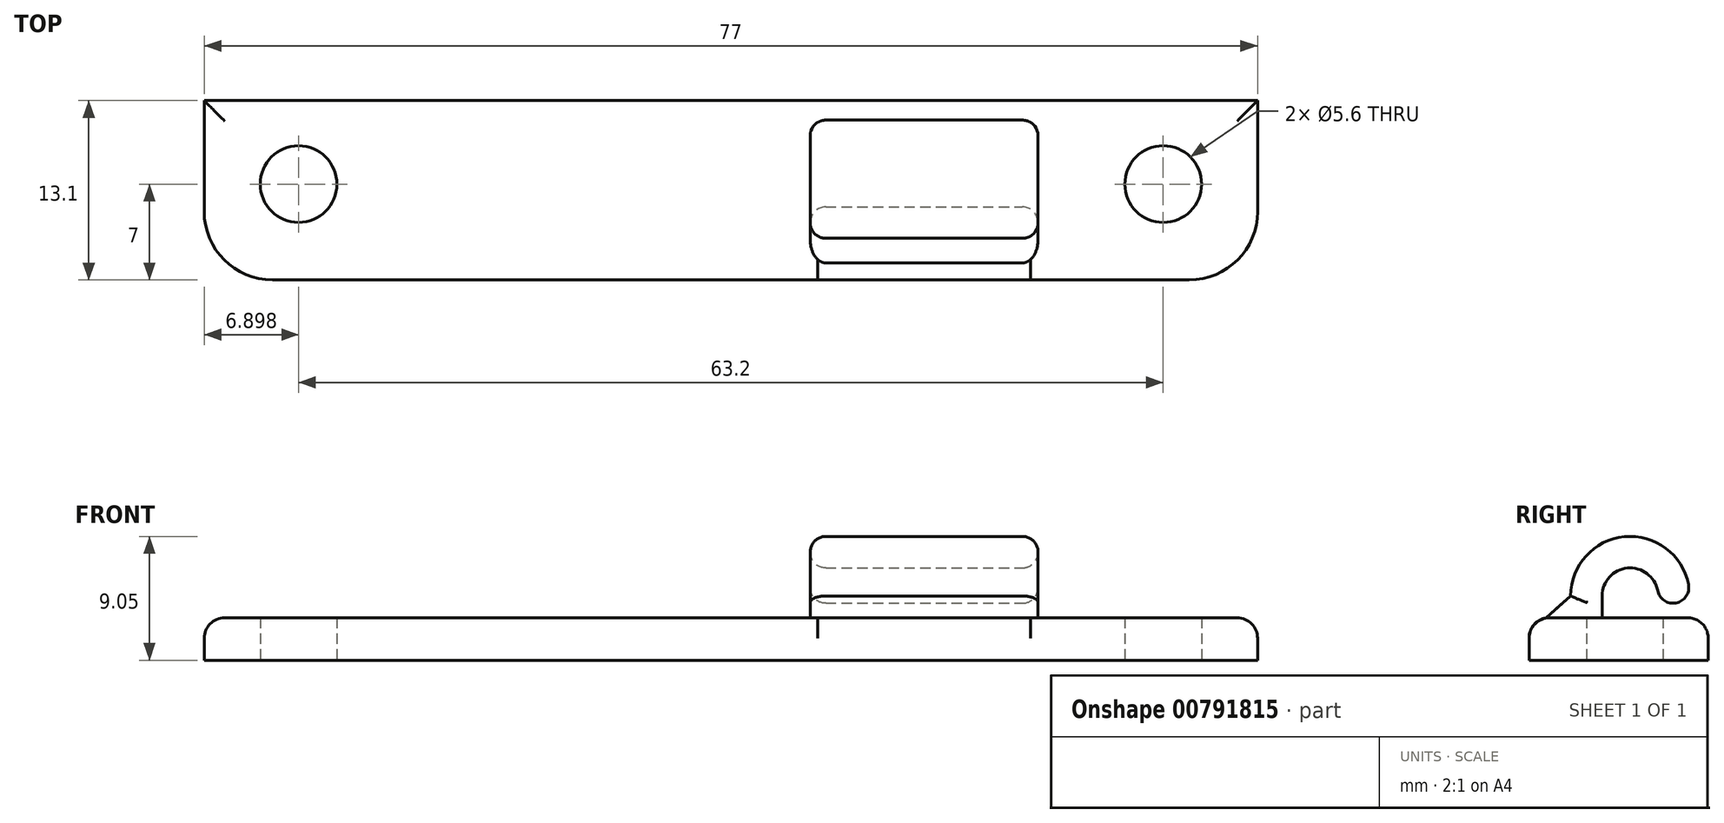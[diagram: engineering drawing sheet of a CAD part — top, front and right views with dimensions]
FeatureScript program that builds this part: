
annotation { "Feature Type Name" : "Feature", "Feature Type Description" : "" }
export const myFeature = defineFeature(function(context is Context, id is Id, definition is map)
    precondition{}
    {
        {
            var Q0;
            Q0=qCreatedBy(makeId("Top.planeOp"),FACE);
            var sketch = newSketch(context, id + "F0", { "sketchPlane" : qUnion([Q0])});
            skLineSegment(sketch, "E0.bottom", {"start": v(-29.06, 27.5) * mm, "end": v(37.94, 27.5) * mm});
            skCircle(sketch, "E1", {"center": v(-27.16, 21.4) * mm, "radius": 2.8 * mm});
            skLineSegment(sketch, "E2", {"start": v(36.74, 27.5) * mm, "end": v(36.74, 21.3) * mm});
            skCircle(sketch, "E3", {"center": v(36.04, 21.4) * mm, "radius": 2.8 * mm});
            skPoint(sketch, "E4.visualSharp", {"position": v(-34.06, 27.5) * mm});
            skPoint(sketch, "E5.visualSharp", {"position": v(42.94, 27.5) * mm});
            skLineSegment(sketch, "E6", {"start": v(-34.06, 27.5) * mm, "end": v(-34.06, 22.5) * mm});
            skLineSegment(sketch, "E7", {"start": v(-29.06, 27.5) * mm, "end": v(-34.06, 27.5) * mm});
            skPoint(sketch, "E8.visualSharp", {"position": v(-34.06, 14.4) * mm});
            skArc(sketch, "E8.filletArc", {"start": v(-34.06, 19.4) * mm, "mid": v(-32.6, 15.86) * mm, "end": v(-29.06, 14.4) * mm});
            skLineSegment(sketch, "E9", {"start": v(37.94, 27.5) * mm, "end": v(42.94, 27.5) * mm});
            skLineSegment(sketch, "E10", {"start": v(42.94, 22.5) * mm, "end": v(42.94, 27.5) * mm});
            skLineSegment(sketch, "E11", {"start": v(-29.06, 14.4) * mm, "end": v(37.94, 14.4) * mm});
            skPoint(sketch, "E12.visualSharp", {"position": v(42.94, 14.4) * mm});
            skArc(sketch, "E12.filletArc", {"start": v(37.94, 14.4) * mm, "mid": v(41.47, 15.86) * mm, "end": v(42.94, 19.4) * mm});
            skLineSegment(sketch, "E13", {"start": v(-34.06, 22.5) * mm, "end": v(-34.06, 19.4) * mm});
            skLineSegment(sketch, "E14", {"start": v(42.94, 22.5) * mm, "end": v(42.94, 19.4) * mm});
            skSolve(sketch);
        }
        {
            var Q0;
            Q0=qSketchRegion(id+"F0",true);
            extrude(context, id + "F1", {"entities" : qUnion([Q0]), "depth" : 3.1 * mm, "offsetDistance" : 25 * mm});
        }
        {
            var Q0;
            Q0=makeQuery(id+"F1.opExtrude","CAP_FACE",FACE,{"disambiguationData":[OSD([sQuery(id+"F0.wireOp",EDGE,"E0.bottom"),sQuery(id+"F0.wireOp",EDGE,"E1"),sQuery(id+"F0.wireOp",EDGE,"E3"),sQuery(id+"F0.wireOp",EDGE,"F014CPc6-vz4U-GeCE-7854-YxV2qlxx2HBI"),sQuery(id+"F0.wireOp",EDGE,"oqsTX8BA-GUAt-ULMf-udCf-k8zS8YHXaQx7"),sQuery(id+"F0.wireOp",EDGE,"E6"),sQuery(id+"F0.wireOp",EDGE,"E7"),sQuery(id+"F0.wireOp",EDGE,"E8.filletArc"),sQuery(id+"F0.wireOp",EDGE,"E9"),sQuery(id+"F0.wireOp",EDGE,"E10"),sQuery(id+"F0.wireOp",EDGE,"boUDxhqq-Myw8-zXRC-cQ7O-OSDsYNN7bkR1"),sQuery(id+"F0.wireOp",EDGE,"Qmjh4y7b-Kf5U-xwWD-JW0z-h2leIeaRO661"),sQuery(id+"F0.wireOp",EDGE,"AKGd9Xzg-GUwK-bWbS-QEfH-SZGkE9dWEIcB"),sQuery(id+"F0.wireOp",EDGE,"A2VAHK38-QV2u-fNEz-uaTx-NxCy4vqKou6f"),sQuery(id+"F0.wireOp",EDGE,"0aa0c002-397a-412f-b6f0-cecf4b393b0d.filletArc"),sQuery(id+"F0.wireOp",EDGE,"e087cdcd-00e5-4b3d-8e79-89354ac833ec.filletArc"),sQuery(id+"F0.wireOp",EDGE,"1e3fda17-eca6-43e5-b7fb-2e88497f6e6a.filletArc")])],"isStart":false});
            var sketch = newSketch(context, id + "F2", { "sketchPlane" : qUnion([Q0])});
            skLineSegment(sketch, "E15.bottom", {"start": v(10.24, 19.74) * mm, "end": v(26.89, 19.74) * mm});
            skLineSegment(sketch, "E15.top", {"start": v(10.24, 17.44) * mm, "end": v(26.89, 17.44) * mm});
            skLineSegment(sketch, "E15.left", {"start": v(10.24, 19.74) * mm, "end": v(10.24, 17.44) * mm});
            skLineSegment(sketch, "E15.right", {"start": v(26.89, 19.74) * mm, "end": v(26.89, 17.44) * mm});
            skSolve(sketch);
        }
        {
            var Q0;
            Q0=qSketchRegion(id+"F2",true);
            extrude(context, id + "F3", {"entities" : qUnion([Q0]), "operationType" : NewBodyOperationType.ADD, "depth" : 1.6 * mm, "offsetDistance" : 25 * mm});
        }
        {
            var Q0;
            Q0=makeQuery(id+"F3.opExtrude","CAP_FACE",FACE,{"disambiguationData":[OSD([sQuery(id+"F2.wireOp",EDGE,"E15.bottom"),sQuery(id+"F2.wireOp",EDGE,"E15.top"),sQuery(id+"F2.wireOp",EDGE,"E15.left"),sQuery(id+"F2.wireOp",EDGE,"E15.right")])],"isStart":false});
            var sketch = newSketch(context, id + "F4", { "sketchPlane" : qUnion([Q0])});
            skLineSegment(sketch, "E16", {"start": v(10.24, 21.79) * mm, "end": v(26.89, 21.79) * mm});
            skSolve(sketch);
        }
        {
            var Q0;
            Q0=makeQuery(id+"F3.opExtrude","CAP_FACE",FACE,{"disambiguationData":[OSD([sQuery(id+"F2.wireOp",EDGE,"E15.bottom"),sQuery(id+"F2.wireOp",EDGE,"E15.top"),sQuery(id+"F2.wireOp",EDGE,"E15.left"),sQuery(id+"F2.wireOp",EDGE,"E15.right")])],"isStart":false});
            var Q1;
            Q1=sQuery(id+"F4.wireOp",EDGE,"E16");
            revolve(context, id + "F5", {"operationType" : NewBodyOperationType.ADD, "surfaceOperationType" : NewSurfaceOperationType.NEW, "entities" : qUnion([Q0]), "axis" : qUnion([Q1]), "revolveType" : RevolveType.ONE_DIRECTION, "oppositeDirection" : true, "angle" : 190 * degree});
        }
        {
            var Q0;
            Q0=makeQuery(id+"F5.opRevolve","CAP_EDGE",EDGE,{"disambiguationData":[OSD([sQuery(id+"F2.wireOp",EDGE,"E15.bottom")])],"isStart":false});
            var Q1;
            Q1=makeQuery(id+"F5.opRevolve","CAP_EDGE",EDGE,{"disambiguationData":[OSD([sQuery(id+"F2.wireOp",EDGE,"E15.top")])],"isStart":false});
            fillet(context, id + "F6", {"entities" : qUnion([Q0, Q1]), "radius" : 1.15 * mm, "tangentPropagation" : true, "allowEdgeOverflow" : false});
        }
        {
            var Q0;
            {var subQ0=sQuery(id+"F2.wireOp",EDGE,"E15.left");Q0=makeQuery(id+"F5.boolean.opBoolean","MERGE",FACE,{"derivedFrom":[makeQuery(id+"F3.opExtrude","SWEPT_FACE",FACE,{"disambiguationData":[OSD([subQ0])]}),makeQuery(id+"F5.opRevolve","SWEPT_FACE",FACE,{"disambiguationData":[OSD([subQ0])]})]});}
            var sketch = newSketch(context, id + "F7", { "sketchPlane" : qUnion([Q0])});
            skLineSegment(sketch, "E17", {"start": v(-17.44, 4.7) * mm, "end": v(-15.64, 3.1) * mm});
            skLineSegment(sketch, "E18", {"start": v(-15.64, 3.1) * mm, "end": v(-17.44, 3.1) * mm});
            skLineSegment(sketch, "E19", {"start": v(-17.44, 4.7) * mm, "end": v(-17.44, 3.1) * mm});
            skSolve(sketch);
        }
        {
            var Q0;
            Q0=qSketchRegion(id+"F7",true);
            extrude(context, id + "F8", {"entities" : qUnion([Q0]), "operationType" : NewBodyOperationType.ADD, "oppositeDirection" : true, "depth" : 16.65 * mm, "offsetDistance" : 25 * mm});
        }
        {
            var Q0;
            Q0=makeQuery(id+"F8.opExtrude","CAP_EDGE",EDGE,{"disambiguationData":[OSD([sQuery(id+"F7.wireOp",EDGE,"E17")])],"isStart":true});
            var Q1;
            Q1=makeQuery(id+"F5.opRevolve","SWEPT_EDGE",EDGE,{"disambiguationData":[OSD([sQuery(id+"F2.wireOp",EDGE,"E15.top"),sQuery(id+"F2.wireOp",EDGE,"E15.left")])]});
            var Q2;
            Q2=makeQuery(id+"F8.opExtrude","CAP_EDGE",EDGE,{"disambiguationData":[OSD([sQuery(id+"F7.wireOp",EDGE,"E17")])],"isStart":false});
            var Q3;
            Q3=makeQuery(id+"F5.opRevolve","SWEPT_EDGE",EDGE,{"disambiguationData":[OSD([sQuery(id+"F2.wireOp",EDGE,"E15.top"),sQuery(id+"F2.wireOp",EDGE,"E15.right")])]});
            fillet(context, id + "F9", {"entities" : qUnion([Q0, Q1, Q2, Q3]), "radius" : 1.14 * mm, "tangentPropagation" : true, "allowEdgeOverflow" : false});
        }
        {
            var Q0;
            Q0=makeQuery(id+"F1.opExtrude","CAP_EDGE",EDGE,{"disambiguationData":[OSD([sQuery(id+"F0.wireOp",EDGE,"E11")])],"isStart":false});
            var Q1;
            Q1=makeQuery(id+"F1.opExtrude","CAP_EDGE",EDGE,{"disambiguationData":[OSD([sQuery(id+"F0.wireOp",EDGE,"E0.bottom"),sQuery(id+"F0.wireOp",EDGE,"E7"),sQuery(id+"F0.wireOp",EDGE,"E9")])],"isStart":false});
            fillet(context, id + "F10", {"entities" : qUnion([Q0, Q1]), "radius" : 1.5 * mm, "tangentPropagation" : true, "allowEdgeOverflow" : false});
        }
    });
